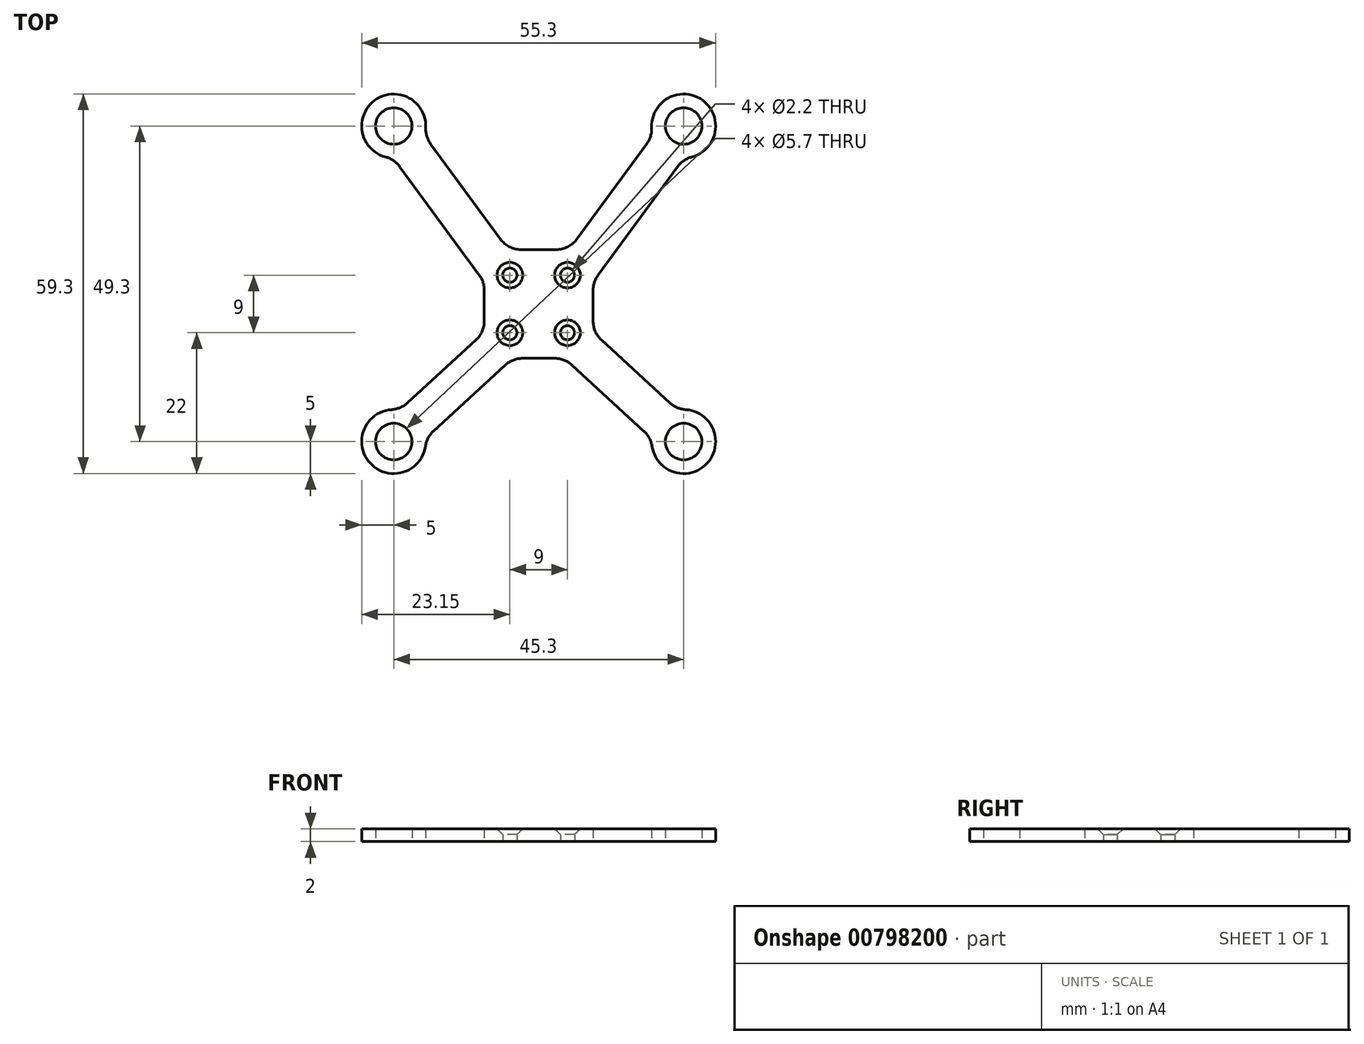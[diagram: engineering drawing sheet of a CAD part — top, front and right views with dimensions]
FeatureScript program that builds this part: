
annotation { "Feature Type Name" : "Feature", "Feature Type Description" : "" }
export const myFeature = defineFeature(function(context is Context, id is Id, definition is map)
    precondition{}
    {
        {
            var Q0;
            Q0=qCreatedBy(makeId("Top.planeOp"),FACE);
            var sketch = newSketch(context, id + "F0", { "sketchPlane" : qUnion([Q0])});
            skLineSegment(sketch, "E0.bottom", {"start": v(14.65, 24.65) * mm, "end": v(-14.65, 24.65) * mm});
            skLineSegment(sketch, "E0.top", {"start": v(14.65, -24.65) * mm, "end": v(-14.65, -24.65) * mm});
            skLineSegment(sketch, "E0.left", {"start": v(14.65, 24.65) * mm, "end": v(14.65, -24.65) * mm});
            skLineSegment(sketch, "E0.right", {"start": v(-14.65, 24.65) * mm, "end": v(-14.65, -24.65) * mm});
            skPoint(sketch, "E0.middle", {"position": v(0, 0) * mm});
            skLineSegment(sketch, "E1.bottom", {"start": v(4.5, 1.35) * mm, "end": v(-4.5, 1.35) * mm});
            skLineSegment(sketch, "E1.top", {"start": v(4.5, -7.65) * mm, "end": v(-4.5, -7.65) * mm});
            skLineSegment(sketch, "E1.left", {"start": v(4.5, 1.35) * mm, "end": v(4.5, -7.65) * mm});
            skLineSegment(sketch, "E1.right", {"start": v(-4.5, 1.35) * mm, "end": v(-4.5, -7.65) * mm});
            skPoint(sketch, "E1.middle", {"position": v(0, -3.15) * mm});
            skSolve(sketch);
        }
        {
            var Q0;
            Q0=qCreatedBy(makeId("Top.planeOp"),FACE);
            var sketch = newSketch(context, id + "F1", { "sketchPlane" : qUnion([Q0])});
            skLineSegment(sketch, "E2.bottom", {"start": v(8.5, 5.35) * mm, "end": v(-8.5, 5.35) * mm, "construction": true});
            skLineSegment(sketch, "E2.top", {"start": v(8.5, -11.65) * mm, "end": v(-8.5, -11.65) * mm, "construction": true});
            skLineSegment(sketch, "E2.left", {"start": v(8.5, 5.35) * mm, "end": v(8.5, -11.65) * mm, "construction": true});
            skLineSegment(sketch, "E2.right", {"start": v(-8.5, 5.35) * mm, "end": v(-8.5, -11.65) * mm, "construction": true});
            skPoint(sketch, "E2.middle", {"position": v(0, -3.15) * mm});
            skCircle(sketch, "E3", {"center": v(-4.5, 1.35) * mm, "radius": 1.1 * mm});
            skCircle(sketch, "E4", {"center": v(4.5, 1.35) * mm, "radius": 1.1 * mm});
            skCircle(sketch, "E5", {"center": v(4.5, -7.65) * mm, "radius": 1.1 * mm});
            skCircle(sketch, "E6", {"center": v(-4.5, -7.65) * mm, "radius": 1.1 * mm});
            skCircle(sketch, "E7", {"center": v(-22.65, -24.65) * mm, "radius": 2.85 * mm});
            skCircle(sketch, "E8", {"center": v(-22.65, -24.65) * mm, "radius": 5 * mm, "construction": true});
            skCircle(sketch, "E9.MirrorC", {"center": v(22.65, -24.65) * mm, "radius": 2.85 * mm});
            skCircle(sketch, "E10.MirrorC", {"center": v(22.65, -24.65) * mm, "radius": 5 * mm, "construction": true});
            skCircle(sketch, "E11.MirrorC", {"center": v(22.65, 24.65) * mm, "radius": 2.85 * mm});
            skCircle(sketch, "E12.MirrorC", {"center": v(22.65, 24.65) * mm, "radius": 5 * mm, "construction": true});
            skCircle(sketch, "E13.MirrorC", {"center": v(-22.65, 24.65) * mm, "radius": 2.85 * mm});
            skCircle(sketch, "E14.MirrorC", {"center": v(-22.65, 24.65) * mm, "radius": 5 * mm, "construction": true});
            skLineSegment(sketch, "E15", {"start": v(-22.65, 24.65) * mm, "end": v(-8.5, 5.35) * mm, "construction": true});
            skLineSegment(sketch, "E16", {"start": v(8.5, 5.35) * mm, "end": v(22.65, 24.65) * mm, "construction": true});
            skLineSegment(sketch, "E17", {"start": v(8.5, -11.65) * mm, "end": v(22.65, -24.65) * mm, "construction": true});
            skLineSegment(sketch, "E18", {"start": v(-8.5, -11.65) * mm, "end": v(-22.65, -24.65) * mm, "construction": true});
            skLineSegment(sketch, "E19", {"start": v(-21.73, -19.73) * mm, "end": v(-8.5, -7.58) * mm});
            skLineSegment(sketch, "E20", {"start": v(-17.67, -24.15) * mm, "end": v(-4.07, -11.65) * mm});
            skLineSegment(sketch, "E21", {"start": v(-22.7, 19.65) * mm, "end": v(-8.5, 0.28) * mm});
            skLineSegment(sketch, "E22", {"start": v(-4.78, 5.35) * mm, "end": v(-17.87, 23.2) * mm});
            skLineSegment(sketch, "E23", {"start": v(-14.9, 9) * mm, "end": v(-10.06, 12.55) * mm, "construction": true});
            skLineSegment(sketch, "E24", {"start": v(-8.74, -15.94) * mm, "end": v(-12.8, -11.52) * mm, "construction": true});
            skPoint(sketch, "E25", {"position": v(-12.48, 10.78) * mm});
            skPoint(sketch, "E26", {"position": v(-10.77, -13.73) * mm});
            skLineSegment(sketch, "E27.MirrorCS", {"start": v(17.67, -24.15) * mm, "end": v(4.07, -11.65) * mm});
            skLineSegment(sketch, "E28.MirrorCS", {"start": v(21.73, -19.73) * mm, "end": v(8.5, -7.58) * mm});
            skLineSegment(sketch, "E29.MirrorCS", {"start": v(22.7, 19.65) * mm, "end": v(8.5, 0.28) * mm});
            skLineSegment(sketch, "E30.MirrorCS", {"start": v(4.78, 5.35) * mm, "end": v(17.87, 23.2) * mm});
            skLineSegment(sketch, "E31", {"start": v(-4.78, 5.35) * mm, "end": v(4.78, 5.35) * mm});
            skLineSegment(sketch, "E32", {"start": v(8.5, 0.28) * mm, "end": v(8.5, -7.58) * mm});
            skLineSegment(sketch, "E33", {"start": v(4.07, -11.65) * mm, "end": v(-4.07, -11.65) * mm});
            skLineSegment(sketch, "E34", {"start": v(-8.5, -7.58) * mm, "end": v(-8.5, 0.28) * mm});
            skArc(sketch, "E35", {"start": v(-17.67, -24.15) * mm, "mid": v(-26.33, -28.03) * mm, "end": v(-21.73, -19.73) * mm});
            skArc(sketch, "E36", {"start": v(21.73, -19.73) * mm, "mid": v(26.33, -28.03) * mm, "end": v(17.67, -24.15) * mm});
            skArc(sketch, "E37", {"start": v(22.7, 19.65) * mm, "mid": v(25.6, 28.68) * mm, "end": v(17.87, 23.2) * mm});
            skArc(sketch, "E38", {"start": v(-17.87, 23.2) * mm, "mid": v(-25.6, 28.68) * mm, "end": v(-22.7, 19.65) * mm});
            skSolve(sketch);
        }
        {
            var Q0;
            Q0=qSketchRegion(id+"F1",true);
            extrude(context, id + "F2", {"entities" : qUnion([Q0]), "depth" : 2 * mm, "offsetDistance" : 25 * mm});
        }
        {
            var Q0;
            Q0=makeQuery(id+"F2.opExtrude","SWEPT_EDGE",EDGE,{"disambiguationData":[OSD([sQuery(id+"F1.wireOp",EDGE,"E21"),sQuery(id+"F1.wireOp",EDGE,"E38")])]});
            var Q1;
            Q1=makeQuery(id+"F2.opExtrude","SWEPT_EDGE",EDGE,{"disambiguationData":[OSD([sQuery(id+"F1.wireOp",EDGE,"E21"),sQuery(id+"F1.wireOp",EDGE,"E34")])]});
            var Q2;
            Q2=makeQuery(id+"F2.opExtrude","SWEPT_EDGE",EDGE,{"disambiguationData":[OSD([sQuery(id+"F1.wireOp",EDGE,"E19"),sQuery(id+"F1.wireOp",EDGE,"E34")])]});
            var Q3;
            Q3=makeQuery(id+"F2.opExtrude","SWEPT_EDGE",EDGE,{"disambiguationData":[OSD([sQuery(id+"F1.wireOp",EDGE,"E19"),sQuery(id+"F1.wireOp",EDGE,"E35")])]});
            var Q4;
            Q4=makeQuery(id+"F2.opExtrude","SWEPT_EDGE",EDGE,{"disambiguationData":[OSD([sQuery(id+"F1.wireOp",EDGE,"E20"),sQuery(id+"F1.wireOp",EDGE,"E35")])]});
            var Q5;
            Q5=makeQuery(id+"F2.opExtrude","SWEPT_EDGE",EDGE,{"disambiguationData":[OSD([sQuery(id+"F1.wireOp",EDGE,"E20"),sQuery(id+"F1.wireOp",EDGE,"E33")])]});
            var Q6;
            Q6=makeQuery(id+"F2.opExtrude","SWEPT_EDGE",EDGE,{"disambiguationData":[OSD([sQuery(id+"F1.wireOp",EDGE,"E27.MirrorCS"),sQuery(id+"F1.wireOp",EDGE,"E33")])]});
            var Q7;
            Q7=makeQuery(id+"F2.opExtrude","SWEPT_EDGE",EDGE,{"disambiguationData":[OSD([sQuery(id+"F1.wireOp",EDGE,"E27.MirrorCS"),sQuery(id+"F1.wireOp",EDGE,"E36")])]});
            var Q8;
            Q8=makeQuery(id+"F2.opExtrude","SWEPT_EDGE",EDGE,{"disambiguationData":[OSD([sQuery(id+"F1.wireOp",EDGE,"E28.MirrorCS"),sQuery(id+"F1.wireOp",EDGE,"E36")])]});
            var Q9;
            Q9=makeQuery(id+"F2.opExtrude","SWEPT_EDGE",EDGE,{"disambiguationData":[OSD([sQuery(id+"F1.wireOp",EDGE,"E28.MirrorCS"),sQuery(id+"F1.wireOp",EDGE,"E32")])]});
            var Q10;
            Q10=makeQuery(id+"F2.opExtrude","SWEPT_EDGE",EDGE,{"disambiguationData":[OSD([sQuery(id+"F1.wireOp",EDGE,"E29.MirrorCS"),sQuery(id+"F1.wireOp",EDGE,"E32")])]});
            var Q11;
            Q11=makeQuery(id+"F2.opExtrude","SWEPT_EDGE",EDGE,{"disambiguationData":[OSD([sQuery(id+"F1.wireOp",EDGE,"E29.MirrorCS"),sQuery(id+"F1.wireOp",EDGE,"E37")])]});
            var Q12;
            Q12=makeQuery(id+"F2.opExtrude","SWEPT_EDGE",EDGE,{"disambiguationData":[OSD([sQuery(id+"F1.wireOp",EDGE,"E30.MirrorCS"),sQuery(id+"F1.wireOp",EDGE,"E37")])]});
            var Q13;
            Q13=makeQuery(id+"F2.opExtrude","SWEPT_EDGE",EDGE,{"disambiguationData":[OSD([sQuery(id+"F1.wireOp",EDGE,"E30.MirrorCS"),sQuery(id+"F1.wireOp",EDGE,"E31")])]});
            var Q14;
            Q14=makeQuery(id+"F2.opExtrude","SWEPT_EDGE",EDGE,{"disambiguationData":[OSD([sQuery(id+"F1.wireOp",EDGE,"E22"),sQuery(id+"F1.wireOp",EDGE,"E31")])]});
            var Q15;
            Q15=makeQuery(id+"F2.opExtrude","SWEPT_EDGE",EDGE,{"disambiguationData":[OSD([sQuery(id+"F1.wireOp",EDGE,"E22"),sQuery(id+"F1.wireOp",EDGE,"E38")])]});
            fillet(context, id + "F3", {"entities" : qUnion([Q0, Q1, Q2, Q3, Q4, Q5, Q6, Q7, Q8, Q9, Q10, Q11, Q12, Q13, Q14, Q15]), "radius" : 4 * mm, "tangentPropagation" : true, "allowEdgeOverflow" : false});
        }
        {
            var Q0;
            Q0=makeQuery(id+"F2.opExtrude","CAP_EDGE",EDGE,{"disambiguationData":[OSD([sQuery(id+"F1.wireOp",EDGE,"E3")])],"isStart":false});
            var Q1;
            Q1=makeQuery(id+"F2.opExtrude","CAP_EDGE",EDGE,{"disambiguationData":[OSD([sQuery(id+"F1.wireOp",EDGE,"E4")])],"isStart":false});
            var Q2;
            Q2=makeQuery(id+"F2.opExtrude","CAP_EDGE",EDGE,{"disambiguationData":[OSD([sQuery(id+"F1.wireOp",EDGE,"E5")])],"isStart":false});
            var Q3;
            Q3=makeQuery(id+"F2.opExtrude","CAP_EDGE",EDGE,{"disambiguationData":[OSD([sQuery(id+"F1.wireOp",EDGE,"E6")])],"isStart":false});
            chamfer(context, id + "F4", {"entities" : qUnion([Q0, Q1, Q2, Q3]), "width" : .9 * mm, "tangentPropagation" : true});
        }
    });
